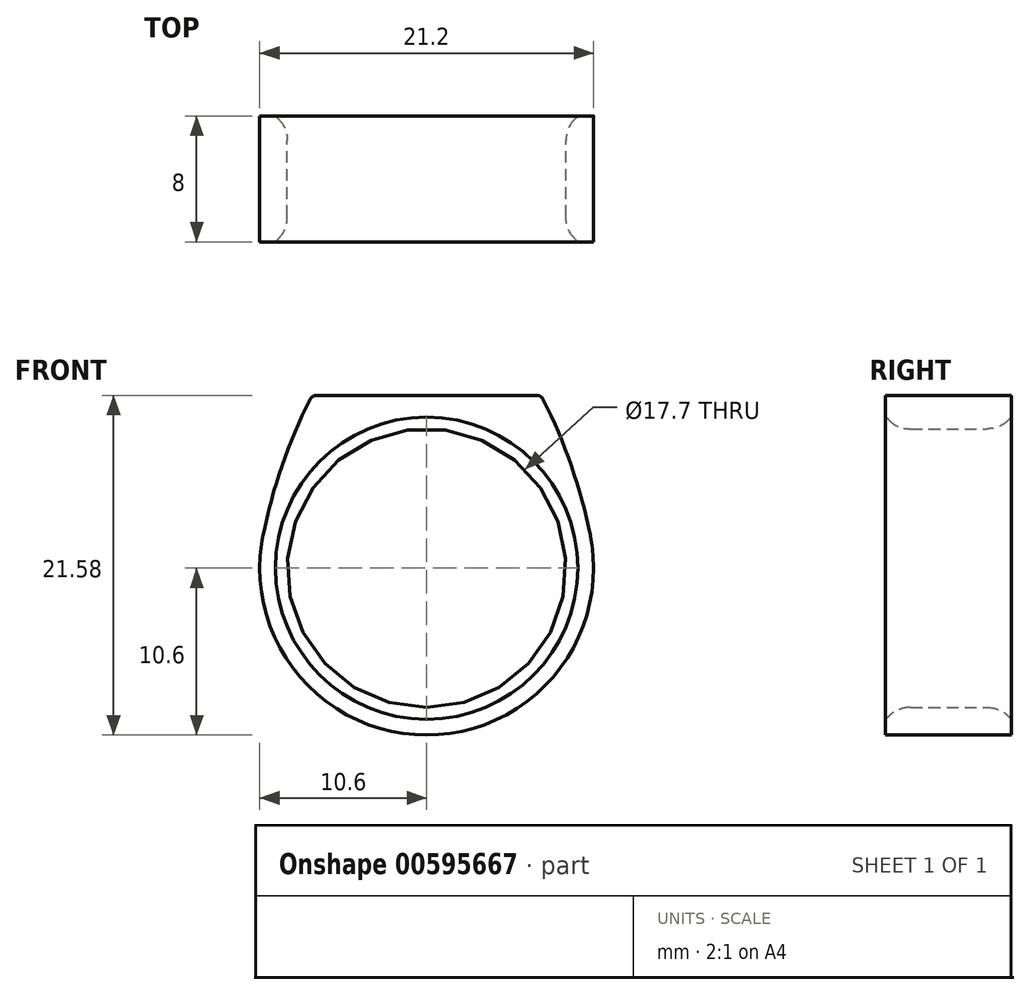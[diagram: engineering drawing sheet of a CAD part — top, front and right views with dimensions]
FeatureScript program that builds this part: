
annotation { "Feature Type Name" : "Feature", "Feature Type Description" : "" }
export const myFeature = defineFeature(function(context is Context, id is Id, definition is map)
    precondition{}
    {
        {
            var Q0;
            Q0=qCreatedBy(makeId("Front.planeOp"),FACE);
            var sketch = newSketch(context, id + "F0", { "sketchPlane" : qUnion([Q0])});
            skCircle(sketch, "E0", {"center": v(0, 0) * mm, "radius": 8.85 * mm});
            skCircle(sketch, "E1.0", {"center": v(0, 0) * mm, "radius": 10.6 * mm});
            skLineSegment(sketch, "E2", {"start": v(-7.27, 10.98) * mm, "end": v(0, 10.98) * mm});
            skLineSegment(sketch, "E3.MirrorCS", {"start": v(7.27, 10.98) * mm, "end": v(0, 10.98) * mm});
            skArc(sketch, "E4", {"start": v(-7.27, 10.98) * mm, "mid": v(-9.16, 6.58) * mm, "end": v(-10.42, 1.95) * mm});
            skArc(sketch, "E5.MirrorCS", {"start": v(7.27, 10.98) * mm, "mid": v(9.16, 6.58) * mm, "end": v(10.42, 1.95) * mm});
            skSolve(sketch);
        }
        {
            var Q0;
            Q0=makeQuery(id+"F0.imprint","IMPRINT",FACE,{"disambiguationData":[TD([[makeQuery(id+"F0.imprint","IMPRINT",EDGE,{"derivedFrom":sQuery(id+"F0.wireOp",EDGE,"E0")}),-1.0]])]});
            var Q1;
            {var subQ1=sQuery(id+"F0.wireOp",EDGE,"E2");Q1=makeQuery(id+"F0.imprint","IMPRINT",FACE,{"disambiguationData":[TD([[makeQuery(id+"F0.imprint","IMPRINT",EDGE,{"derivedFrom":subQ1}),-1.0]])]});}
            extrude(context, id + "F1", {"entities" : qUnion([Q0, Q1]), "depth" : 4 * mm, "offsetDistance" : 25 * mm, "hasSecondDirection" : true, "secondDirectionOppositeDirection" : true, "secondDirectionDepth" : 4 * mm});
        }
        {
            var Q0;
            Q0=makeQuery(id+"F1.opExtrude","SWEPT_EDGE",EDGE,{"disambiguationData":[OSD([sQuery(id+"F0.wireOp",EDGE,"E1.0"),sQuery(id+"F0.wireOp",EDGE,"E4")])]});
            var Q1;
            Q1=makeQuery(id+"F1.opExtrude","SWEPT_EDGE",EDGE,{"disambiguationData":[OSD([sQuery(id+"F0.wireOp",EDGE,"E1.0"),sQuery(id+"F0.wireOp",EDGE,"E5.MirrorCS")])]});
            fillet(context, id + "F2", {"entities" : qUnion([Q0, Q1]), "radius" : 10 * mm, "tangentPropagation" : true, "allowEdgeOverflow" : false});
        }
        {
            var Q0;
            Q0=makeQuery(id+"F1.opExtrude","CAP_EDGE",EDGE,{"disambiguationData":[OSD([sQuery(id+"F0.wireOp",EDGE,"E0")])],"isStart":true});
            var Q1;
            Q1=makeQuery(id+"F1.opExtrude","CAP_EDGE",EDGE,{"disambiguationData":[OSD([sQuery(id+"F0.wireOp",EDGE,"E0")])],"isStart":false});
            chamfer(context, id + "F3", {"entities" : qUnion([Q0, Q1]), "width" : .75 * mm, "tangentPropagation" : true});
        }
        {
            var Q0;
            Q0=makeQuery(id+"F1.opExtrude","SWEPT_EDGE",EDGE,{"disambiguationData":[OSD([sQuery(id+"F0.wireOp",EDGE,"E2"),sQuery(id+"F0.wireOp",EDGE,"E4")])]});
            var Q1;
            Q1=makeQuery(id+"F1.opExtrude","SWEPT_EDGE",EDGE,{"disambiguationData":[OSD([sQuery(id+"F0.wireOp",EDGE,"E3.MirrorCS"),sQuery(id+"F0.wireOp",EDGE,"E5.MirrorCS")])]});
            fillet(context, id + "F4", {"entities" : qUnion([Q0, Q1]), "radius" : 0.47 * mm, "tangentPropagation" : true, "allowEdgeOverflow" : false});
        }
        {
            var Q0;
            {var subQ0=sQuery(id+"F0.wireOp",EDGE,"E0");Q0=makeQuery(id+"F3.opChamfer","BLEND_EDGE",EDGE,{"blendedFrom":[makeQuery(id+"F1.opExtrude","CAP_EDGE",EDGE,{"disambiguationData":[OSD([subQ0])],"isStart":false}),makeQuery(id+"F1.opExtrude","SWEPT_FACE",FACE,{"disambiguationData":[OSD([subQ0])]})],"blendedInto":[makeQuery(id+"F1.opExtrude","SWEPT_FACE",FACE,{"disambiguationData":[OSD([subQ0])]})]});}
            var Q1;
            {var subQ0=sQuery(id+"F0.wireOp",EDGE,"E0");Q1=makeQuery(id+"F3.opChamfer","BLEND_EDGE",EDGE,{"blendedFrom":[makeQuery(id+"F1.opExtrude","CAP_EDGE",EDGE,{"disambiguationData":[OSD([subQ0])],"isStart":true}),makeQuery(id+"F1.opExtrude","SWEPT_FACE",FACE,{"disambiguationData":[OSD([subQ0])]})],"blendedInto":[makeQuery(id+"F1.opExtrude","SWEPT_FACE",FACE,{"disambiguationData":[OSD([subQ0])]})]});}
            fillet(context, id + "F5", {"entities" : qUnion([Q0, Q1]), "radius" : 2 * mm, "tangentPropagation" : true, "rho" : 0.5, "crossSection" : FilletCrossSection.CONIC, "allowEdgeOverflow" : false});
        }
    });
